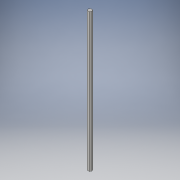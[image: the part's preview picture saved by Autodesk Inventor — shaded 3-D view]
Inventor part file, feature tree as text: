
AUTODESK INVENTOR PART (.ipt)
format: ipt  version: 2016 (Build 200138000, 138)  size: 92,160 bytes
history: native  units: in
note: dims shown in document units (in); Inventor stores cm internally (conversion verified against a paired STEP export)
features: extrude x1, sketch x1
ambient origin geometry x8: Origin, YZ Plane, XZ Plane, XY Plane, X Axis, Y Axis, Z Axis, Center Point
bodies: Solid1 (feature_tree)
feature tree (2):
  extrude  "Extrusion1"  Depth=20.0in TaperAngle=0.0deg
  sketch  "Sketch1"  dims[d0=0.5in d1=20.0in d2=0.0in]
